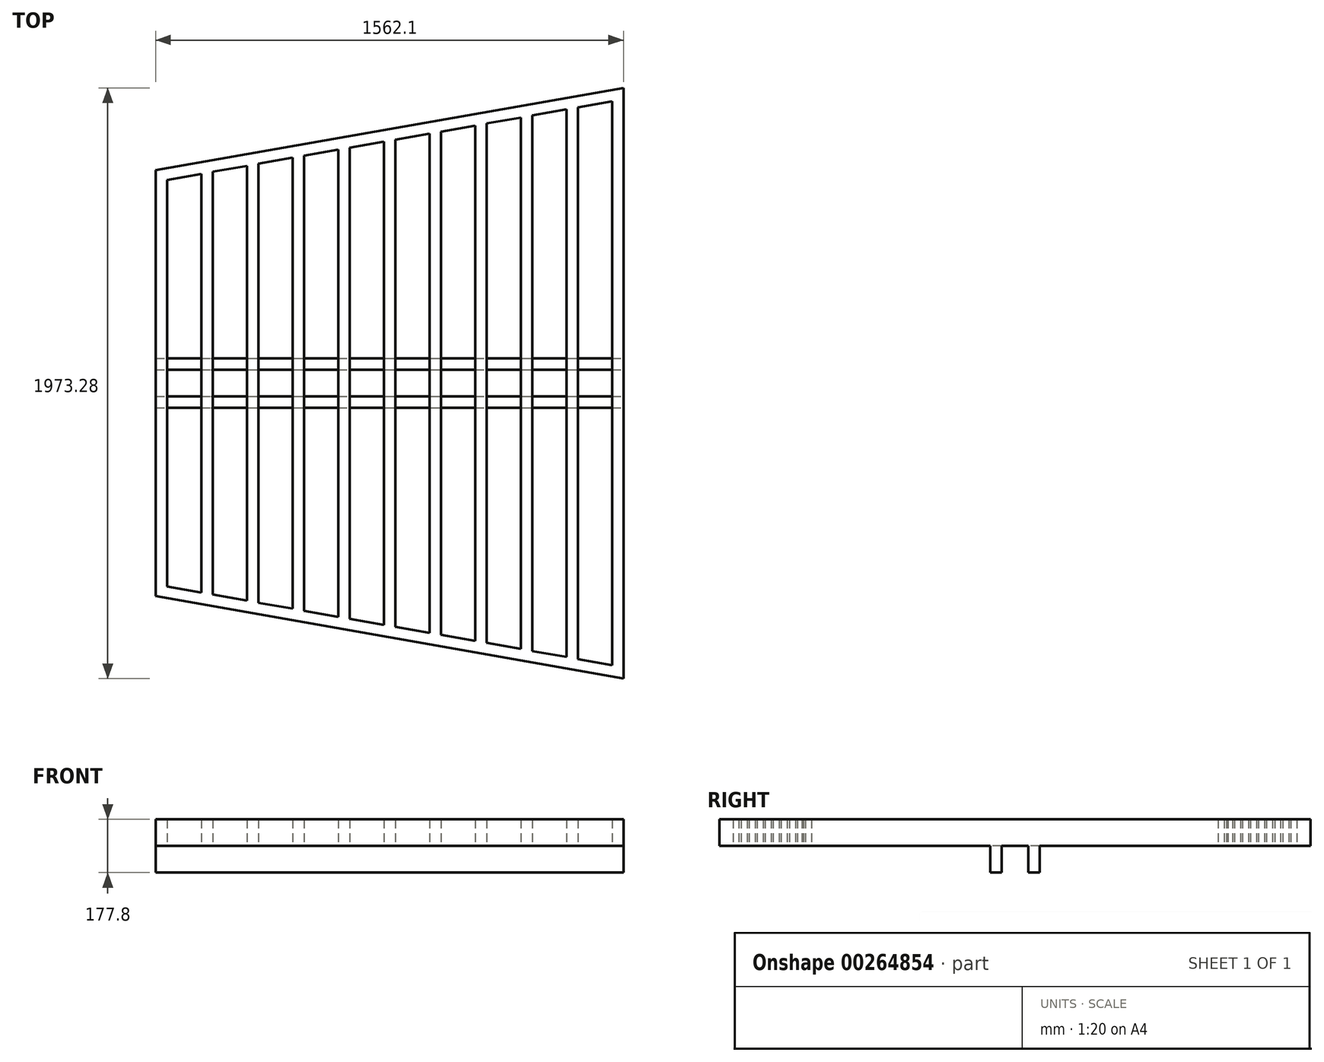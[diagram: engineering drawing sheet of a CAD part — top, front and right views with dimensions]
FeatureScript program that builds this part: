
annotation { "Feature Type Name" : "Feature", "Feature Type Description" : "" }
export const myFeature = defineFeature(function(context is Context, id is Id, definition is map)
    precondition{}
    {
        {
            var Q0;
            Q0=qCreatedBy(makeId("Top.planeOp"),FACE);
            var sketch = newSketch(context, id + "F0", { "sketchPlane" : qUnion([Q0])});
            skLineSegment(sketch, "E0.left", {"start": v(535.49, 1079.39) * mm, "end": v(535.49, 406.88) * mm});
            skLineSegment(sketch, "E0.right", {"start": v(573.59, 1086.1) * mm, "end": v(573.59, 406.88) * mm});
            skLineSegment(sketch, "E1", {"start": v(573.59, 1086.1) * mm, "end": v(687.89, 1106.26) * mm});
            skLineSegment(sketch, "E2", {"start": v(535.49, 1118.08) * mm, "end": v(2097.59, 1393.52) * mm});
            skLineSegment(sketch, "E3.1.0.0", {"start": v(687.89, 1106.26) * mm, "end": v(687.89, 406.88) * mm});
            skLineSegment(sketch, "E3.1.0.1", {"start": v(725.99, 1112.98) * mm, "end": v(725.99, 406.88) * mm});
            skLineSegment(sketch, "E3.2.0.0", {"start": v(840.29, 1133.13) * mm, "end": v(840.29, 406.88) * mm});
            skLineSegment(sketch, "E3.2.0.1", {"start": v(878.39, 1139.85) * mm, "end": v(878.39, 406.88) * mm});
            skLineSegment(sketch, "E3.3.0.0", {"start": v(992.69, 1160) * mm, "end": v(992.69, 406.88) * mm});
            skLineSegment(sketch, "E3.3.0.1", {"start": v(1030.79, 1166.72) * mm, "end": v(1030.79, 406.88) * mm});
            skLineSegment(sketch, "E3.4.0.0", {"start": v(1145.09, 1186.88) * mm, "end": v(1145.09, 406.88) * mm});
            skLineSegment(sketch, "E3.4.0.1", {"start": v(1183.19, 1193.6) * mm, "end": v(1183.19, 406.88) * mm});
            skLineSegment(sketch, "E3.5.0.0", {"start": v(1297.49, 1213.75) * mm, "end": v(1297.49, 406.88) * mm});
            skLineSegment(sketch, "E3.5.0.1", {"start": v(1335.59, 1220.47) * mm, "end": v(1335.59, 406.88) * mm});
            skLineSegment(sketch, "E3.6.0.0", {"start": v(1449.89, 1240.62) * mm, "end": v(1449.89, 406.88) * mm});
            skLineSegment(sketch, "E3.6.0.1", {"start": v(1487.99, 1247.34) * mm, "end": v(1487.99, 406.88) * mm});
            skLineSegment(sketch, "E3.7.0.0", {"start": v(1602.29, 1267.5) * mm, "end": v(1602.29, 406.88) * mm});
            skLineSegment(sketch, "E3.7.0.1", {"start": v(1640.39, 1274.21) * mm, "end": v(1640.39, 406.88) * mm});
            skLineSegment(sketch, "E3.8.0.0", {"start": v(1754.69, 1294.37) * mm, "end": v(1754.69, 406.88) * mm});
            skLineSegment(sketch, "E3.8.0.1", {"start": v(1792.79, 1301.09) * mm, "end": v(1792.79, 406.88) * mm});
            skLineSegment(sketch, "E3.9.0.0", {"start": v(1907.09, 1321.24) * mm, "end": v(1907.09, 406.88) * mm});
            skLineSegment(sketch, "E3.9.0.1", {"start": v(1945.19, 1327.96) * mm, "end": v(1945.19, 406.88) * mm});
            skLineSegment(sketch, "E3.10.0.0", {"start": v(2059.49, 1348.11) * mm, "end": v(2059.49, 406.88) * mm});
            skLineSegment(sketch, "E3.10.0.1", {"start": v(2097.59, 1354.83) * mm, "end": v(2097.59, 406.88) * mm});
            skLineSegment(sketch, "E4", {"start": v(2097.59, 1393.52) * mm, "end": v(2097.59, 1354.83) * mm});
            skLineSegment(sketch, "E5", {"start": v(535.49, 1079.39) * mm, "end": v(535.49, 1118.08) * mm});
            skLineSegment(sketch, "E6", {"start": v(535.49, 406.88) * mm, "end": v(573.59, 406.88) * mm});
            skLineSegment(sketch, "E7.trimOffspring", {"start": v(725.99, 1112.98) * mm, "end": v(840.29, 1133.13) * mm});
            skLineSegment(sketch, "E8.trimOffspring", {"start": v(878.39, 1139.85) * mm, "end": v(992.69, 1160) * mm});
            skLineSegment(sketch, "E9.trimOffspring", {"start": v(1030.79, 1166.72) * mm, "end": v(1145.09, 1186.88) * mm});
            skLineSegment(sketch, "E10.trimOffspring", {"start": v(1183.19, 1193.6) * mm, "end": v(1297.49, 1213.75) * mm});
            skLineSegment(sketch, "E11.trimOffspring", {"start": v(1335.59, 1220.47) * mm, "end": v(1449.89, 1240.62) * mm});
            skLineSegment(sketch, "E12.trimOffspring", {"start": v(1487.99, 1247.34) * mm, "end": v(1602.29, 1267.5) * mm});
            skLineSegment(sketch, "E13.trimOffspring", {"start": v(1640.39, 1274.21) * mm, "end": v(1754.69, 1294.37) * mm});
            skLineSegment(sketch, "E14.trimOffspring", {"start": v(1792.79, 1301.09) * mm, "end": v(1907.09, 1321.24) * mm});
            skLineSegment(sketch, "E15.trimOffspring", {"start": v(1945.19, 1327.96) * mm, "end": v(2059.49, 1348.11) * mm});
            skLineSegment(sketch, "E16.trimOffspring", {"start": v(687.89, 406.88) * mm, "end": v(725.99, 406.88) * mm});
            skLineSegment(sketch, "E17.trimOffspring", {"start": v(840.29, 406.88) * mm, "end": v(878.39, 406.88) * mm});
            skLineSegment(sketch, "E18.trimOffspring", {"start": v(992.69, 406.88) * mm, "end": v(1030.79, 406.88) * mm});
            skLineSegment(sketch, "E19.trimOffspring", {"start": v(1145.09, 406.88) * mm, "end": v(1183.19, 406.88) * mm});
            skLineSegment(sketch, "E20.trimOffspring", {"start": v(1297.49, 406.88) * mm, "end": v(1335.59, 406.88) * mm});
            skLineSegment(sketch, "E21.trimOffspring", {"start": v(1449.89, 406.88) * mm, "end": v(1487.99, 406.88) * mm});
            skLineSegment(sketch, "E22.trimOffspring", {"start": v(1602.29, 406.88) * mm, "end": v(1640.39, 406.88) * mm});
            skLineSegment(sketch, "E23.trimOffspring", {"start": v(1754.69, 406.88) * mm, "end": v(1792.79, 406.88) * mm});
            skLineSegment(sketch, "E24.trimOffspring", {"start": v(1907.09, 406.88) * mm, "end": v(1945.19, 406.88) * mm});
            skLineSegment(sketch, "E25.trimOffspring", {"start": v(2059.49, 406.88) * mm, "end": v(2097.59, 406.88) * mm});
            skSolve(sketch);
        }
        {
            var Q0;
            Q0=makeQuery(id+"F0.imprint","IMPRINT",FACE,{"disambiguationData":[TD([[makeQuery(id+"F0.imprint","IMPRINT",EDGE,{"derivedFrom":sQuery(id+"F0.wireOp",EDGE,"E2")}),-1.0]])]});
            var Q1;
            {var subQ2=sQuery(id+"F0.wireOp",EDGE,"E0.left");Q1=makeQuery(id+"F0.imprint","IMPRINT",FACE,{"disambiguationData":[TD([[makeQuery(id+"F0.imprint","IMPRINT",EDGE,{"derivedFrom":subQ2}),1.0]])]});}
            var Q2;
            {var subQ1=sQuery(id+"F0.wireOp",EDGE,"E3.1.0.1");Q2=makeQuery(id+"F0.imprint","IMPRINT",FACE,{"disambiguationData":[TD([[makeQuery(id+"F0.imprint","IMPRINT",EDGE,{"derivedFrom":subQ1}),-1.0]])]});}
            var Q3;
            {var subQ1=sQuery(id+"F0.wireOp",EDGE,"E3.2.0.0");Q3=makeQuery(id+"F0.imprint","IMPRINT",FACE,{"disambiguationData":[TD([[makeQuery(id+"F0.imprint","IMPRINT",EDGE,{"derivedFrom":subQ1}),1.0]])]});}
            var Q4;
            {var subQ1=sQuery(id+"F0.wireOp",EDGE,"E3.3.0.0");Q4=makeQuery(id+"F0.imprint","IMPRINT",FACE,{"disambiguationData":[TD([[makeQuery(id+"F0.imprint","IMPRINT",EDGE,{"derivedFrom":subQ1}),1.0]])]});}
            var Q5;
            {var subQ1=sQuery(id+"F0.wireOp",EDGE,"E3.4.0.0");Q5=makeQuery(id+"F0.imprint","IMPRINT",FACE,{"disambiguationData":[TD([[makeQuery(id+"F0.imprint","IMPRINT",EDGE,{"derivedFrom":subQ1}),1.0]])]});}
            var Q6;
            {var subQ1=sQuery(id+"F0.wireOp",EDGE,"E3.5.0.0");Q6=makeQuery(id+"F0.imprint","IMPRINT",FACE,{"disambiguationData":[TD([[makeQuery(id+"F0.imprint","IMPRINT",EDGE,{"derivedFrom":subQ1}),1.0]])]});}
            var Q7;
            {var subQ1=sQuery(id+"F0.wireOp",EDGE,"E3.6.0.0");Q7=makeQuery(id+"F0.imprint","IMPRINT",FACE,{"disambiguationData":[TD([[makeQuery(id+"F0.imprint","IMPRINT",EDGE,{"derivedFrom":subQ1}),1.0]])]});}
            var Q8;
            {var subQ1=sQuery(id+"F0.wireOp",EDGE,"E3.7.0.0");Q8=makeQuery(id+"F0.imprint","IMPRINT",FACE,{"disambiguationData":[TD([[makeQuery(id+"F0.imprint","IMPRINT",EDGE,{"derivedFrom":subQ1}),1.0]])]});}
            var Q9;
            {var subQ1=sQuery(id+"F0.wireOp",EDGE,"E3.8.0.0");Q9=makeQuery(id+"F0.imprint","IMPRINT",FACE,{"disambiguationData":[TD([[makeQuery(id+"F0.imprint","IMPRINT",EDGE,{"derivedFrom":subQ1}),1.0]])]});}
            var Q10;
            {var subQ1=sQuery(id+"F0.wireOp",EDGE,"E3.9.0.0");Q10=makeQuery(id+"F0.imprint","IMPRINT",FACE,{"disambiguationData":[TD([[makeQuery(id+"F0.imprint","IMPRINT",EDGE,{"derivedFrom":subQ1}),1.0]])]});}
            var Q11;
            {var subQ3=sQuery(id+"F0.wireOp",EDGE,"E3.10.0.0");Q11=makeQuery(id+"F0.imprint","IMPRINT",FACE,{"disambiguationData":[TD([[makeQuery(id+"F0.imprint","IMPRINT",EDGE,{"derivedFrom":subQ3}),1.0]])]});}
            var Q12;
            Q12=makeQuery(id+"F0.imprint","IMPRINT",FACE,{"disambiguationData":[TD([[makeQuery(id+"F0.imprint","IMPRINT",EDGE,{"derivedFrom":sQuery(id+"F0.wireOp",EDGE,"d747dd7a-df65-4655-8c56-110b9610b72c0.MirrorCS")}),1.0]])]});
            extrude(context, id + "F1", {"entities" : qUnion([Q0, Q1, Q2, Q3, Q4, Q5, Q6, Q7, Q8, Q9, Q10, Q11, Q12]), "depth" : 88.9 * mm, "offsetDistance" : 25.4 * mm});
        }
        {
            var Q0;
            Q0=makeQuery(id+"F1.opExtrude","SWEPT_BODY",BODY,{"disambiguationData":[OSD([sQuery(id+"F0.wireOp",EDGE,"E0.left"),sQuery(id+"F0.wireOp",EDGE,"E1"),sQuery(id+"F0.wireOp",EDGE,"E2"),sQuery(id+"F0.wireOp",EDGE,"E3.1.0.1"),sQuery(id+"F0.wireOp",EDGE,"E3.2.0.0"),sQuery(id+"F0.wireOp",EDGE,"E3.2.0.1"),sQuery(id+"F0.wireOp",EDGE,"E3.3.0.0"),sQuery(id+"F0.wireOp",EDGE,"E3.3.0.1"),sQuery(id+"F0.wireOp",EDGE,"E3.4.0.0"),sQuery(id+"F0.wireOp",EDGE,"E3.4.0.1"),sQuery(id+"F0.wireOp",EDGE,"E3.5.0.0"),sQuery(id+"F0.wireOp",EDGE,"E3.5.0.1"),sQuery(id+"F0.wireOp",EDGE,"E3.6.0.0"),sQuery(id+"F0.wireOp",EDGE,"E3.6.0.1"),sQuery(id+"F0.wireOp",EDGE,"E3.7.0.0"),sQuery(id+"F0.wireOp",EDGE,"E3.7.0.1"),sQuery(id+"F0.wireOp",EDGE,"E3.8.0.0"),sQuery(id+"F0.wireOp",EDGE,"E3.8.0.1"),sQuery(id+"F0.wireOp",EDGE,"E3.9.0.0"),sQuery(id+"F0.wireOp",EDGE,"E3.9.0.1"),sQuery(id+"F0.wireOp",EDGE,"E3.10.0.0"),sQuery(id+"F0.wireOp",EDGE,"E3.10.0.1"),sQuery(id+"F0.wireOp",EDGE,"E4"),sQuery(id+"F0.wireOp",EDGE,"E0.right"),sQuery(id+"F0.wireOp",EDGE,"E3.1.0.0"),sQuery(id+"F0.wireOp",EDGE,"E5"),sQuery(id+"F0.wireOp",EDGE,"E6"),sQuery(id+"F0.wireOp",EDGE,"E7.trimOffspring"),sQuery(id+"F0.wireOp",EDGE,"E8.trimOffspring"),sQuery(id+"F0.wireOp",EDGE,"E9.trimOffspring"),sQuery(id+"F0.wireOp",EDGE,"E10.trimOffspring"),sQuery(id+"F0.wireOp",EDGE,"E11.trimOffspring"),sQuery(id+"F0.wireOp",EDGE,"E12.trimOffspring"),sQuery(id+"F0.wireOp",EDGE,"E13.trimOffspring"),sQuery(id+"F0.wireOp",EDGE,"E14.trimOffspring"),sQuery(id+"F0.wireOp",EDGE,"E15.trimOffspring"),sQuery(id+"F0.wireOp",EDGE,"E16.trimOffspring"),sQuery(id+"F0.wireOp",EDGE,"E17.trimOffspring"),sQuery(id+"F0.wireOp",EDGE,"E18.trimOffspring"),sQuery(id+"F0.wireOp",EDGE,"E19.trimOffspring"),sQuery(id+"F0.wireOp",EDGE,"E20.trimOffspring"),sQuery(id+"F0.wireOp",EDGE,"E21.trimOffspring"),sQuery(id+"F0.wireOp",EDGE,"E22.trimOffspring"),sQuery(id+"F0.wireOp",EDGE,"E23.trimOffspring"),sQuery(id+"F0.wireOp",EDGE,"E24.trimOffspring"),sQuery(id+"F0.wireOp",EDGE,"E25.trimOffspring")])]});
            var Q1;
            Q1=makeQuery(id+"F1.opExtrude","SWEPT_FACE",FACE,{"disambiguationData":[OSD([sQuery(id+"F0.wireOp",EDGE,"E6")])]});
            mirror(context, id + "F2", {"operationType" : NewBodyOperationType.ADD, "entities" : qUnion([Q0]), "mirrorPlane" : qUnion([Q1])});
        }
        {
            var Q0;
            {var subQ0=makeQuery(id+"F1.opExtrude","SWEPT_FACE",FACE,{"disambiguationData":[OSD([sQuery(id+"F0.wireOp",EDGE,"E3.10.0.1"),sQuery(id+"F0.wireOp",EDGE,"E4")])]});Q0=makeQuery(id+"F2.boolean.opBoolean","MERGE",FACE,{"derivedFrom":[subQ0,makeQuery(id+"F2.opPattern","COPY",FACE,{"derivedFrom":subQ0,"instanceName":"1"})]});}
            var sketch = newSketch(context, id + "F3", { "sketchPlane" : qUnion([Q0])});
            skLineSegment(sketch, "E26", {"start": v(406.88, 88.9) * mm, "end": v(406.88, -233.52) * mm});
            skLineSegment(sketch, "E27.bottom", {"start": v(406.88, -233.52) * mm, "end": v(362.43, -233.52) * mm});
            skLineSegment(sketch, "E27.top", {"start": v(406.88, 0) * mm, "end": v(362.43, 0) * mm});
            skLineSegment(sketch, "E27.left", {"start": v(406.88, -233.52) * mm, "end": v(406.88, 0) * mm});
            skLineSegment(sketch, "E27.right", {"start": v(362.43, -233.52) * mm, "end": v(362.43, 0) * mm});
            skLineSegment(sketch, "E28.bottom", {"start": v(362.43, 0) * mm, "end": v(324.33, 0) * mm});
            skLineSegment(sketch, "E28.top", {"start": v(362.43, -88.9) * mm, "end": v(324.33, -88.9) * mm});
            skLineSegment(sketch, "E28.left", {"start": v(362.43, 0) * mm, "end": v(362.43, -88.9) * mm});
            skLineSegment(sketch, "E28.right", {"start": v(324.33, 0) * mm, "end": v(324.33, -88.9) * mm});
            skLineSegment(sketch, "E29.MirrorCS", {"start": v(451.33, -88.9) * mm, "end": v(489.43, -88.9) * mm});
            skLineSegment(sketch, "E30.MirrorCS", {"start": v(489.43, 0) * mm, "end": v(489.43, -88.9) * mm});
            skLineSegment(sketch, "E31.MirrorCS", {"start": v(451.33, 0) * mm, "end": v(451.33, -88.9) * mm});
            skLineSegment(sketch, "E32.MirrorCS", {"start": v(451.33, 0) * mm, "end": v(489.43, 0) * mm});
            skSolve(sketch);
        }
        {
            var Q0;
            Q0=makeQuery(id+"F3.imprint","IMPRINT",FACE,{"disambiguationData":[TD([[makeQuery(id+"F3.imprint","IMPRINT",EDGE,{"derivedFrom":sQuery(id+"F3.wireOp",EDGE,"E28.bottom")}),1.0]])]});
            var Q1;
            Q1=makeQuery(id+"F3.imprint","IMPRINT",FACE,{"disambiguationData":[TD([[makeQuery(id+"F3.imprint","IMPRINT",EDGE,{"derivedFrom":sQuery(id+"F3.wireOp",EDGE,"E29.MirrorCS")}),1.0]])]});
            var Q2;
            {var subQ0=makeQuery(id+"F1.opExtrude","SWEPT_FACE",FACE,{"disambiguationData":[OSD([sQuery(id+"F0.wireOp",EDGE,"E0.left"),sQuery(id+"F0.wireOp",EDGE,"E5")])]});Q2=makeQuery(id+"F2.boolean.opBoolean","MERGE",FACE,{"derivedFrom":[subQ0,makeQuery(id+"F2.opPattern","COPY",FACE,{"derivedFrom":subQ0,"instanceName":"1"})]});}
            extrude(context, id + "F4", {"entities" : qUnion([Q0, Q1]), "operationType" : NewBodyOperationType.ADD, "endBound" : BoundingType.UP_TO_SURFACE, "oppositeDirection" : true, "depth" : 25.4 * mm, "endBoundEntityFace" : qUnion([Q2]), "offsetDistance" : 25.4 * mm});
        }
    });
